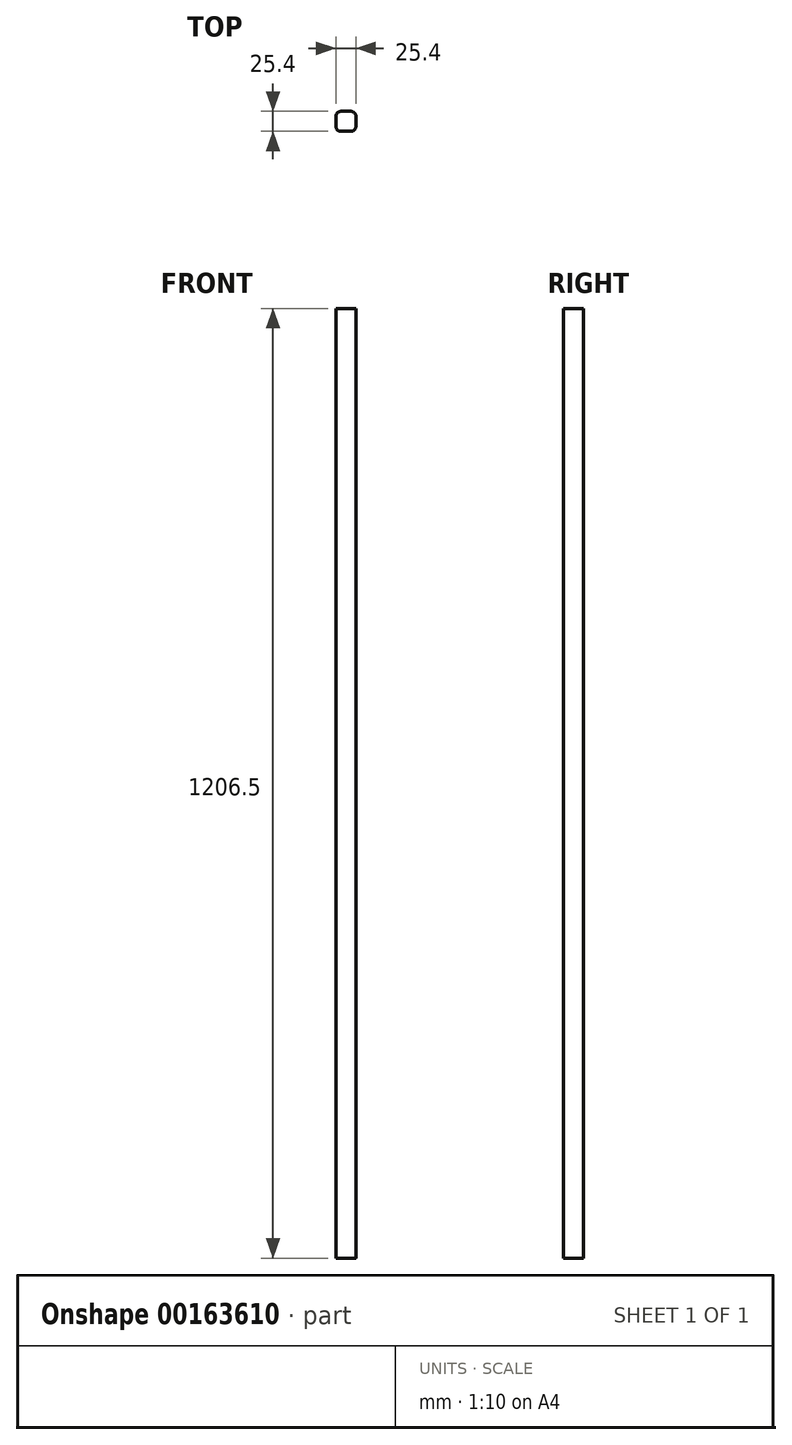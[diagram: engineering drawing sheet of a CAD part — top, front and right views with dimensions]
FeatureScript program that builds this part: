
annotation { "Feature Type Name" : "Feature", "Feature Type Description" : "" }
export const myFeature = defineFeature(function(context is Context, id is Id, definition is map)
    precondition{}
    {
        {
            var Q0;
            Q0=qCreatedBy(makeId("Top.planeOp"),FACE);
            var sketch = newSketch(context, id + "F0", { "sketchPlane" : qUnion([Q0])});
            skLineSegment(sketch, "E0.bottom", {"start": v(6.35, 12.7) * mm, "end": v(-6.35, 12.7) * mm});
            skLineSegment(sketch, "E0.top", {"start": v(6.35, -12.7) * mm, "end": v(-6.35, -12.7) * mm});
            skLineSegment(sketch, "E0.left", {"start": v(12.7, 6.35) * mm, "end": v(12.7, -6.35) * mm});
            skLineSegment(sketch, "E0.right", {"start": v(-12.7, 6.35) * mm, "end": v(-12.7, -6.35) * mm});
            skPoint(sketch, "E0.middle", {"position": v(0, 0) * mm});
            skPoint(sketch, "E1.visualSharp", {"position": v(-12.7, 12.7) * mm});
            skArc(sketch, "E1.filletArc", {"start": v(-6.35, 12.7) * mm, "mid": v(-10.84, 10.84) * mm, "end": v(-12.7, 6.35) * mm});
            skPoint(sketch, "E2.visualSharp", {"position": v(12.7, 12.7) * mm});
            skArc(sketch, "E2.filletArc", {"start": v(12.7, 6.35) * mm, "mid": v(10.84, 10.84) * mm, "end": v(6.35, 12.7) * mm});
            skPoint(sketch, "E3.visualSharp", {"position": v(12.7, -12.7) * mm});
            skArc(sketch, "E3.filletArc", {"start": v(6.35, -12.7) * mm, "mid": v(10.84, -10.84) * mm, "end": v(12.7, -6.35) * mm});
            skPoint(sketch, "E4.visualSharp", {"position": v(-12.7, -12.7) * mm});
            skArc(sketch, "E4.filletArc", {"start": v(-12.7, -6.35) * mm, "mid": v(-10.84, -10.84) * mm, "end": v(-6.35, -12.7) * mm});
            skSolve(sketch);
        }
        {
            var Q0;
            Q0 = qSketchRegion(id + "F0", true);
            extrude(context, id + "F1", {"entities" : qUnion([Q0]), "depth" : 1206.5 * mm});
        }
    });
